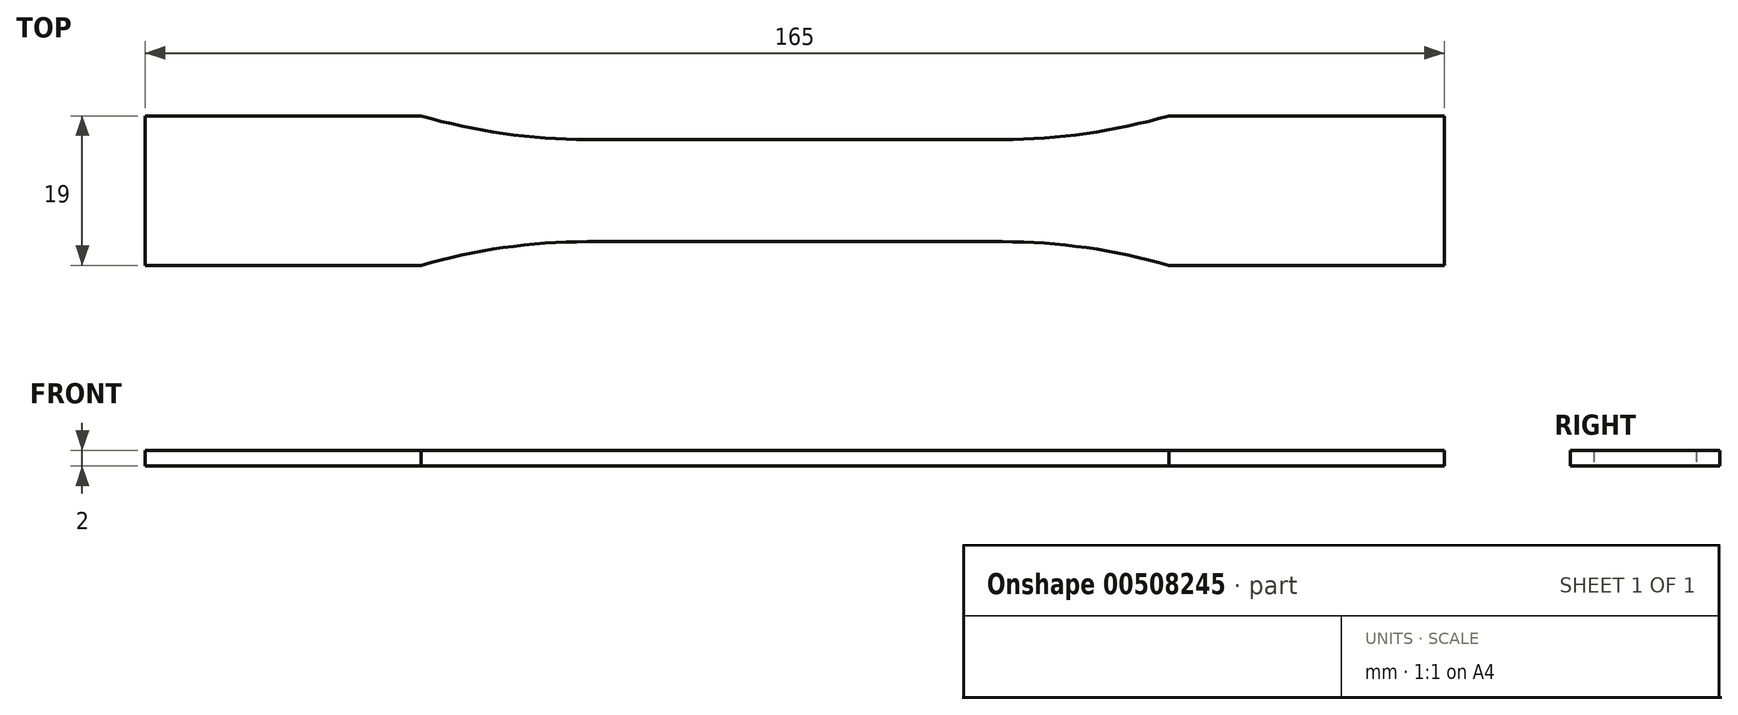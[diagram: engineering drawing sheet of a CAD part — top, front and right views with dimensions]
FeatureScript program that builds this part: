
annotation { "Feature Type Name" : "Feature", "Feature Type Description" : "" }
export const myFeature = defineFeature(function(context is Context, id is Id, definition is map)
    precondition{}
    {
        {
            var Q0;
            Q0=qCreatedBy(makeId("Top.planeOp"),FACE);
            var sketch = newSketch(context, id + "F0", { "sketchPlane" : qUnion([Q0])});
            skLineSegment(sketch, "E0", {"start": v(0, 0) * mm, "end": v(0, -18.62) * mm});
            skLineSegment(sketch, "E1", {"start": v(82.5, 0) * mm, "end": v(0, 0) * mm});
            skLineSegment(sketch, "E2", {"start": v(0, 6.5) * mm, "end": v(26.36, 6.5) * mm});
            skPoint(sketch, "E2.startSnap0", {"position": v(0, -9.3) * mm});
            skLineSegment(sketch, "E3", {"start": v(47.5, 9.5) * mm, "end": v(82.5, 9.5) * mm});
            skLineSegment(sketch, "E4", {"start": v(82.5, 9.5) * mm, "end": v(82.5, 0) * mm});
            skArc(sketch, "E5", {"start": v(26.36, 6.5) * mm, "mid": v(37.03, 7.25) * mm, "end": v(47.5, 9.5) * mm});
            skLineSegment(sketch, "E6.MirrorCS", {"start": v(0, -6.5) * mm, "end": v(26.36, -6.5) * mm});
            skArc(sketch, "E7.MirrorCS", {"start": v(26.36, -6.5) * mm, "mid": v(37.03, -7.25) * mm, "end": v(47.5, -9.5) * mm});
            skLineSegment(sketch, "E8.MirrorCS", {"start": v(47.5, -9.5) * mm, "end": v(82.5, -9.5) * mm});
            skLineSegment(sketch, "E9.MirrorCS", {"start": v(82.5, -9.5) * mm, "end": v(82.5, 0) * mm});
            skLineSegment(sketch, "E10.MirrorCS", {"start": v(0, 6.5) * mm, "end": v(-26.36, 6.5) * mm});
            skLineSegment(sketch, "E11.MirrorCS", {"start": v(0, -6.5) * mm, "end": v(-26.36, -6.5) * mm});
            skArc(sketch, "E12.MirrorCS", {"start": v(-26.36, 6.5) * mm, "mid": v(-37.03, 7.25) * mm, "end": v(-47.5, 9.5) * mm});
            skArc(sketch, "E13.MirrorCS", {"start": v(-26.36, -6.5) * mm, "mid": v(-37.03, -7.25) * mm, "end": v(-47.5, -9.5) * mm});
            skLineSegment(sketch, "E14.MirrorCS", {"start": v(-47.5, -9.5) * mm, "end": v(-82.5, -9.5) * mm});
            skLineSegment(sketch, "E15.MirrorCS", {"start": v(-47.5, 9.5) * mm, "end": v(-82.5, 9.5) * mm});
            skLineSegment(sketch, "E16.MirrorCS", {"start": v(-82.5, 9.5) * mm, "end": v(-82.5, 0) * mm});
            skLineSegment(sketch, "E17.MirrorCS", {"start": v(-82.5, -9.5) * mm, "end": v(-82.5, 0) * mm});
            skSolve(sketch);
        }
        {
            var Q0;
            Q0=qSketchRegion(id+"F0",true);
            extrude(context, id + "F1", {"entities" : qUnion([Q0]), "depth" : 2 * mm});
        }
    });
